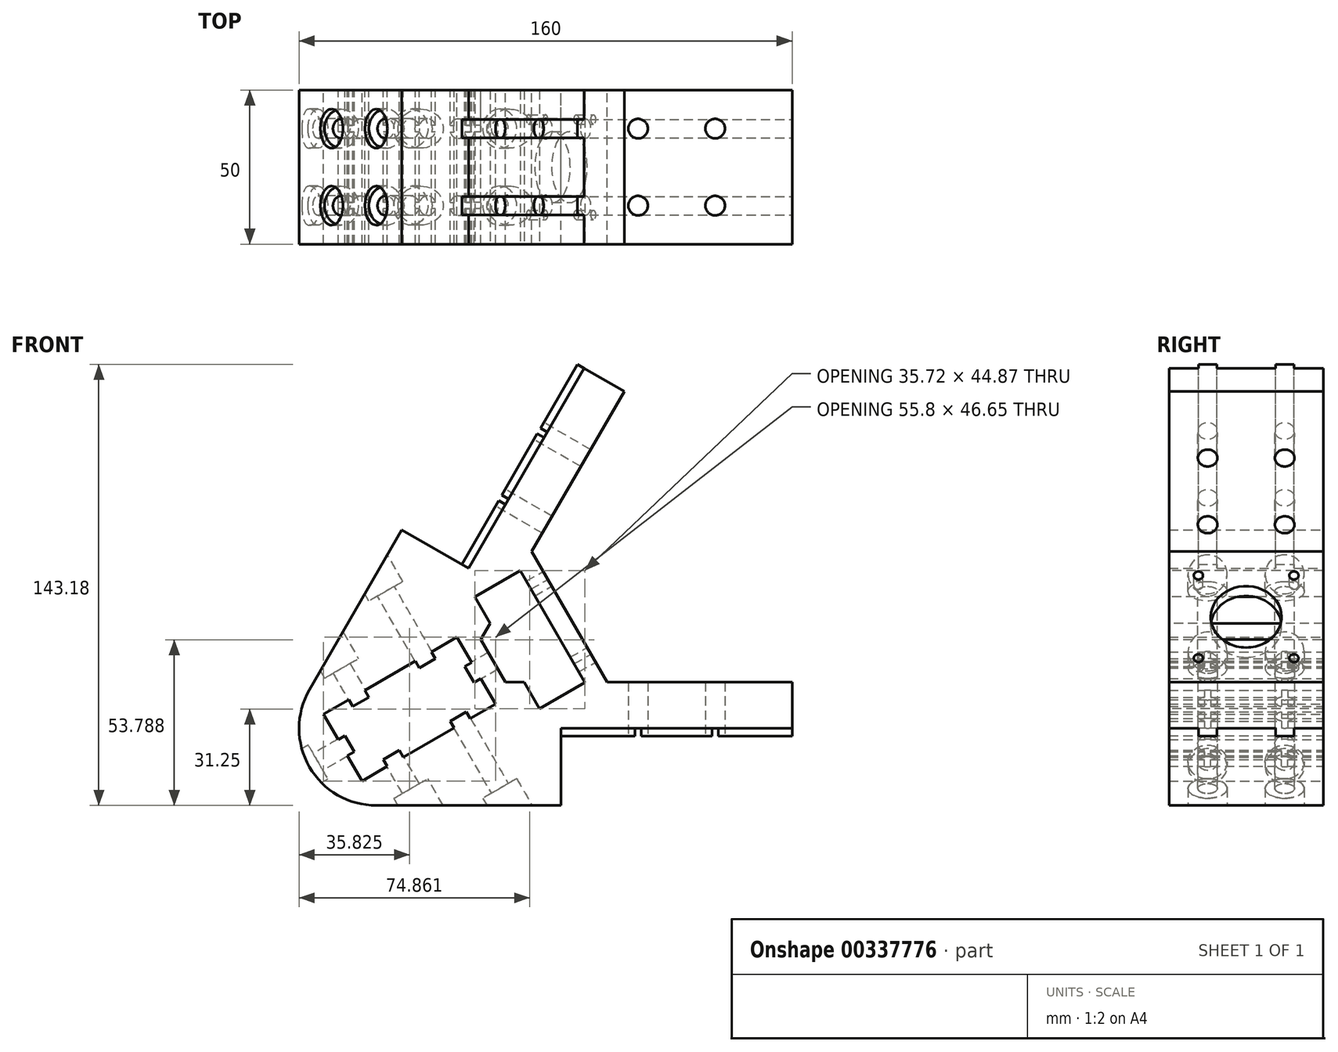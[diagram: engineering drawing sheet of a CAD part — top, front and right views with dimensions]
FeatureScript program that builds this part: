
annotation { "Feature Type Name" : "Feature", "Feature Type Description" : "" }
export const myFeature = defineFeature(function(context is Context, id is Id, definition is map)
    precondition{}
    {
        {
            var Q0;
            Q0=qCreatedBy(makeId("Front.planeOp"),FACE);
            var sketch = newSketch(context, id + "F0", { "sketchPlane" : qUnion([Q0])});
            skLineSegment(sketch, "E0", {"start": v(0, 0) * mm, "end": v(260, 0) * mm, "construction": true});
            skLineSegment(sketch, "E1", {"start": v(0, 0) * mm, "end": v(130, 225.17) * mm, "construction": true});
            skLineSegment(sketch, "E2", {"start": v(60, 0) * mm, "end": v(60, -25) * mm, "construction": true});
            skLineSegment(sketch, "E3", {"start": v(60, -25) * mm, "end": v(260, -25) * mm, "construction": true});
            skLineSegment(sketch, "E4", {"start": v(260, -25) * mm, "end": v(260, 0) * mm, "construction": true});
            skLineSegment(sketch, "E5", {"start": v(30, 51.96) * mm, "end": v(8.35, 64.46) * mm, "construction": true});
            skLineSegment(sketch, "E6", {"start": v(8.35, 64.46) * mm, "end": v(108.35, 237.67) * mm, "construction": true});
            skLineSegment(sketch, "E7", {"start": v(108.35, 237.67) * mm, "end": v(130, 225.17) * mm, "construction": true});
            skLineSegment(sketch, "E8", {"start": v(67.5, 116.91) * mm, "end": v(80.5, 109.41) * mm});
            skLineSegment(sketch, "E9", {"start": v(80.5, 109.41) * mm, "end": v(33.98, 28.85) * mm});
            skLineSegment(sketch, "E10", {"start": v(135, 0) * mm, "end": v(135, 15) * mm});
            skLineSegment(sketch, "E11", {"start": v(135, 15) * mm, "end": v(41.97, 15) * mm});
            skLineSegment(sketch, "E12", {"start": v(0, 0) * mm, "end": v(32.48, 18.75) * mm, "construction": true});
            skLineSegment(sketch, "E13", {"start": v(0, 0) * mm, "end": v(-6.25, 10.83) * mm, "construction": true});
            skLineSegment(sketch, "E14", {"start": v(32.48, 18.75) * mm, "end": v(26.23, 29.58) * mm});
            skLineSegment(sketch, "E15", {"start": v(26.23, 29.58) * mm, "end": v(-6.25, 10.83) * mm});
            skLineSegment(sketch, "E16", {"start": v(-6.25, 10.83) * mm, "end": v(-17.08, 4.58) * mm});
            skLineSegment(sketch, "E17", {"start": v(-17.08, 4.58) * mm, "end": v(-4.58, -17.08) * mm});
            skLineSegment(sketch, "E18", {"start": v(-4.58, -17.08) * mm, "end": v(38.73, 7.92) * mm});
            skLineSegment(sketch, "E19", {"start": v(38.73, 7.92) * mm, "end": v(32.48, 18.75) * mm});
            skArc(sketch, "E20", {"start": v(-21.65, 12.5) * mm, "mid": v(-21.65, -12.5) * mm, "end": v(0, -25) * mm});
            skLineSegment(sketch, "E21", {"start": v(8.35, 64.46) * mm, "end": v(-21.65, 12.5) * mm});
            skLineSegment(sketch, "E22", {"start": v(60, -25) * mm, "end": v(0, -25) * mm});
            skLineSegment(sketch, "E23", {"start": v(30, 51.96) * mm, "end": v(67.5, 116.91) * mm});
            skLineSegment(sketch, "E24", {"start": v(8.35, 64.46) * mm, "end": v(30, 51.96) * mm});
            skLineSegment(sketch, "E25", {"start": v(135, 0) * mm, "end": v(60, 0) * mm});
            skLineSegment(sketch, "E26", {"start": v(60, -25) * mm, "end": v(60, 0) * mm});
            skLineSegment(sketch, "E27", {"start": v(0, 0) * mm, "end": v(0, 0) * mm});
            skLineSegment(sketch, "E28", {"start": v(62.72, 36.21) * mm, "end": v(-21.65, -12.5) * mm});
            skLineSegment(sketch, "E29", {"start": v(50.47, 57.42) * mm, "end": v(74.97, 15) * mm});
            skLineSegment(sketch, "E30", {"start": v(46.8, 51.07) * mm, "end": v(67.64, 15) * mm});
            skLineSegment(sketch, "E31", {"start": v(41.97, 15) * mm, "end": v(33.98, 28.85) * mm});
            skLineSegment(sketch, "E32", {"start": v(46.72, 51.22) * mm, "end": v(32, 42.72) * mm, "construction": true});
            skLineSegment(sketch, "E33", {"start": v(32, 42.72) * mm, "end": v(53, 6.35) * mm, "construction": true});
            skLineSegment(sketch, "E34", {"start": v(53, 6.35) * mm, "end": v(67.72, 14.85) * mm, "construction": true});
            skLineSegment(sketch, "E35", {"start": v(57.22, 33.04) * mm, "end": v(42.5, 24.54) * mm});
            skSolve(sketch);
        }
        {
            var Q0;
            Q0=makeQuery(id+"F0.imprint","IMPRINT",FACE,{"disambiguationData":[TD([[makeQuery(id+"F0.imprint","IMPRINT",EDGE,{"derivedFrom":sQuery(id+"F0.wireOp",EDGE,"E8")}),-1.0]])]});
            var Q1;
            {var subQ0=sQuery(id+"F0.wireOp",EDGE,"E29");var subQ1=sQuery(id+"F0.wireOp",EDGE,"E9");var subQ2=makeQuery(id+"F0.imprint","INTERSECT",VERTEX,{"derivedFrom":[subQ1,subQ0]});Q1=makeQuery(id+"F0.imprint","IMPRINT",FACE,{"disambiguationData":[TD([[makeQuery(id+"F0.imprint","IMPRINT",EDGE,{"disambiguationData":[TD([[subQ2,-1.0]])],"derivedFrom":subQ1}),1.0]])]});}
            extrude(context, id + "F1", {"entities" : qUnion([Q0, Q1]), "depth" : 50 * mm});
        }
        {
            var Q0;
            Q0=makeQuery(id+"F1.opExtrude","CAP_FACE",FACE,{"disambiguationData":[OSD([sQuery(id+"F0.wireOp",EDGE,"E8"),sQuery(id+"F0.wireOp",EDGE,"E9"),sQuery(id+"F0.wireOp",EDGE,"E14"),sQuery(id+"F0.wireOp",EDGE,"E15"),sQuery(id+"F0.wireOp",EDGE,"E16"),sQuery(id+"F0.wireOp",EDGE,"E17"),sQuery(id+"F0.wireOp",EDGE,"E20"),sQuery(id+"F0.wireOp",EDGE,"E21"),sQuery(id+"F0.wireOp",EDGE,"oqZTHpmg-IY26-M5HD-25FB-tw3BaVAHPTJi"),sQuery(id+"F0.wireOp",EDGE,"E23"),sQuery(id+"F0.wireOp",EDGE,"E24"),sQuery(id+"F0.wireOp",EDGE,"E28"),sQuery(id+"F0.wireOp",EDGE,"E29"),sQuery(id+"F0.wireOp",EDGE,"E30"),sQuery(id+"F0.wireOp",EDGE,"hlFoshtQ-Obu4-Otg3-1oye-F89BNM93I3Rv")])],"isStart":true});
            var sketch = newSketch(context, id + "F2", { "sketchPlane" : qUnion([Q0])});
            skLineSegment(sketch, "E36.0", {"start": v(-26.23, 29.58) * mm, "end": v(17.08, 4.58) * mm});
            skLineSegment(sketch, "E37.0", {"start": v(-32.48, 18.75) * mm, "end": v(-26.23, 29.58) * mm});
            skLineSegment(sketch, "E38.0", {"start": v(17.08, 4.58) * mm, "end": v(10.83, -6.25) * mm});
            skLineSegment(sketch, "E39", {"start": v(-12.8, 21.83) * mm, "end": v(-14.07, 19.63) * mm});
            skLineSegment(sketch, "E40", {"start": v(-14.07, 19.63) * mm, "end": v(-19.27, 22.63) * mm});
            skLineSegment(sketch, "E41", {"start": v(-19.27, 22.63) * mm, "end": v(-18, 24.83) * mm});
            skLineSegment(sketch, "E42", {"start": v(-16.67, 21.13) * mm, "end": v(-15.4, 23.33) * mm});
            skLineSegment(sketch, "E43", {"start": v(10.83, -6.25) * mm, "end": v(8.63, -4.98) * mm});
            skLineSegment(sketch, "E44", {"start": v(8.63, -4.98) * mm, "end": v(10.13, -2.38) * mm});
            skLineSegment(sketch, "E45", {"start": v(10.13, -2.38) * mm, "end": v(12.33, -3.65) * mm});
            skLineSegment(sketch, "E46", {"start": v(-32.48, 18.75) * mm, "end": v(-30.28, 17.48) * mm});
            skLineSegment(sketch, "E47", {"start": v(-30.28, 17.48) * mm, "end": v(-28.78, 20.08) * mm});
            skLineSegment(sketch, "E48", {"start": v(-28.78, 20.08) * mm, "end": v(-30.98, 21.35) * mm});
            skLineSegment(sketch, "E49", {"start": v(8.85, 9.33) * mm, "end": v(7.58, 7.13) * mm});
            skLineSegment(sketch, "E50", {"start": v(7.58, 7.13) * mm, "end": v(2.38, 10.13) * mm});
            skLineSegment(sketch, "E51", {"start": v(2.38, 10.13) * mm, "end": v(3.65, 12.33) * mm});
            skLineSegment(sketch, "E52", {"start": v(4.98, 8.63) * mm, "end": v(6.25, 10.83) * mm});
            skSolve(sketch);
        }
        {
            var Q0;
            {var subQ0=sQuery(id+"F2.wireOp",EDGE,"E41");Q0=makeQuery(id+"F2.imprint","IMPRINT",FACE,{"disambiguationData":[TD([[makeQuery(id+"F2.imprint","IMPRINT",EDGE,{"derivedFrom":subQ0}),-1.0]])]});}
            var Q1;
            {var subQ0=sQuery(id+"F2.wireOp",EDGE,"E39");Q1=makeQuery(id+"F2.imprint","IMPRINT",FACE,{"disambiguationData":[TD([[makeQuery(id+"F2.imprint","IMPRINT",EDGE,{"derivedFrom":subQ0}),-1.0]])]});}
            var Q2;
            {var subQ0=sQuery(id+"F2.wireOp",EDGE,"E46");Q2=makeQuery(id+"F2.imprint","IMPRINT",FACE,{"disambiguationData":[TD([[makeQuery(id+"F2.imprint","IMPRINT",EDGE,{"derivedFrom":subQ0}),1.0]])]});}
            var Q3;
            {var subQ0=sQuery(id+"F2.wireOp",EDGE,"E43");Q3=makeQuery(id+"F2.imprint","IMPRINT",FACE,{"disambiguationData":[TD([[makeQuery(id+"F2.imprint","IMPRINT",EDGE,{"derivedFrom":subQ0}),-1.0]])]});}
            var Q4;
            {var subQ0=sQuery(id+"F2.wireOp",EDGE,"E51");Q4=makeQuery(id+"F2.imprint","IMPRINT",FACE,{"disambiguationData":[TD([[makeQuery(id+"F2.imprint","IMPRINT",EDGE,{"derivedFrom":subQ0}),-1.0]])]});}
            var Q5;
            {var subQ0=sQuery(id+"F2.wireOp",EDGE,"E49");Q5=makeQuery(id+"F2.imprint","IMPRINT",FACE,{"disambiguationData":[TD([[makeQuery(id+"F2.imprint","IMPRINT",EDGE,{"derivedFrom":subQ0}),-1.0]])]});}
            var Q6;
            Q6=makeQuery(id+"F1.opExtrude","CAP_FACE",FACE,{"disambiguationData":[OSD([sQuery(id+"F0.wireOp",EDGE,"E8"),sQuery(id+"F0.wireOp",EDGE,"E9"),sQuery(id+"F0.wireOp",EDGE,"E14"),sQuery(id+"F0.wireOp",EDGE,"E15"),sQuery(id+"F0.wireOp",EDGE,"E16"),sQuery(id+"F0.wireOp",EDGE,"E17"),sQuery(id+"F0.wireOp",EDGE,"E20"),sQuery(id+"F0.wireOp",EDGE,"E21"),sQuery(id+"F0.wireOp",EDGE,"oqZTHpmg-IY26-M5HD-25FB-tw3BaVAHPTJi"),sQuery(id+"F0.wireOp",EDGE,"E23"),sQuery(id+"F0.wireOp",EDGE,"E24"),sQuery(id+"F0.wireOp",EDGE,"E28"),sQuery(id+"F0.wireOp",EDGE,"E29"),sQuery(id+"F0.wireOp",EDGE,"E30"),sQuery(id+"F0.wireOp",EDGE,"hlFoshtQ-Obu4-Otg3-1oye-F89BNM93I3Rv")])],"isStart":false});
            extrude(context, id + "F3", {"entities" : qUnion([Q0, Q1, Q2, Q3, Q4, Q5]), "operationType" : NewBodyOperationType.ADD, "endBound" : BoundingType.UP_TO_SURFACE, "oppositeDirection" : true, "endBoundEntityFace" : qUnion([Q6]), "depth" : 25.4 * mm, "offsetDistance" : 25.4 * mm});
        }
        {
            var Q0;
            Q0=makeQuery(id+"F1.opExtrude","SWEPT_FACE",FACE,{"disambiguationData":[OSD([sQuery(id+"F0.wireOp",EDGE,"E23")])]});
            var sketch = newSketch(context, id + "F4", { "sketchPlane" : qUnion([Q0])});
            skLineSegment(sketch, "E53.bottom", {"start": v(15.5, 60) * mm, "end": v(9.5, 60) * mm});
            skLineSegment(sketch, "E53.top", {"start": v(15.5, 135) * mm, "end": v(9.5, 135) * mm});
            skLineSegment(sketch, "E53.left", {"start": v(15.5, 60) * mm, "end": v(15.5, 135) * mm});
            skLineSegment(sketch, "E53.right", {"start": v(9.5, 60) * mm, "end": v(9.5, 135) * mm});
            skPoint(sketch, "E53.middle", {"position": v(12.5, 97.5) * mm});
            skLineSegment(sketch, "E54.bottom", {"start": v(34.5, 60) * mm, "end": v(40.5, 60) * mm});
            skLineSegment(sketch, "E54.top", {"start": v(34.5, 135) * mm, "end": v(40.5, 135) * mm});
            skLineSegment(sketch, "E54.left", {"start": v(40.5, 60) * mm, "end": v(40.5, 135) * mm});
            skLineSegment(sketch, "E54.right", {"start": v(34.5, 60) * mm, "end": v(34.5, 135) * mm});
            skPoint(sketch, "E54.middle", {"position": v(37.5, 97.5) * mm});
            skSolve(sketch);
        }
        {
            var Q0;
            Q0 = qSketchRegion(id + "F4", true);
            extrude(context, id + "F5", {"entities" : qUnion([Q0]), "operationType" : NewBodyOperationType.ADD, "depth" : 2.54 * mm});
        }
        {
            var Q0;
            Q0=makeQuery(id+"F5.opExtrude","CAP_FACE",FACE,{"disambiguationData":[OSD([sQuery(id+"F4.wireOp",EDGE,"E53.bottom"),sQuery(id+"F4.wireOp",EDGE,"E53.top"),sQuery(id+"F4.wireOp",EDGE,"E53.left"),sQuery(id+"F4.wireOp",EDGE,"E53.right")])],"isStart":false});
            var sketch = newSketch(context, id + "F6", { "sketchPlane" : qUnion([Q0])});
            skLineSegment(sketch, "E55", {"start": v(12.5, 60) * mm, "end": v(12.5, 85) * mm});
            skLineSegment(sketch, "E56", {"start": v(12.5, 85) * mm, "end": v(12.5, 110) * mm});
            skLineSegment(sketch, "E57", {"start": v(12.5, 110) * mm, "end": v(12.5, 135) * mm});
            skLineSegment(sketch, "E58.0", {"start": v(40.5, 60) * mm, "end": v(34.5, 60) * mm});
            skLineSegment(sketch, "E59.0", {"start": v(40.5, 135) * mm, "end": v(34.5, 135) * mm});
            skLineSegment(sketch, "E60", {"start": v(37.5, 60) * mm, "end": v(37.5, 85) * mm});
            skLineSegment(sketch, "E61", {"start": v(37.5, 85) * mm, "end": v(37.5, 110) * mm});
            skLineSegment(sketch, "E62", {"start": v(37.5, 110) * mm, "end": v(37.5, 135) * mm});
            skCircle(sketch, "E63", {"center": v(12.5, 85) * mm, "radius": 3.18 * mm});
            skCircle(sketch, "E64", {"center": v(12.5, 110) * mm, "radius": 3.18 * mm});
            skCircle(sketch, "E65", {"center": v(37.5, 110) * mm, "radius": 3.18 * mm});
            skCircle(sketch, "E66", {"center": v(37.5, 85) * mm, "radius": 3.18 * mm});
            skSolve(sketch);
        }
        {
            var Q0;
            Q0 = qSketchRegion(id + "F6", true);
            extrude(context, id + "F7", {"entities" : qUnion([Q0]), "operationType" : NewBodyOperationType.REMOVE, "endBound" : BoundingType.THROUGH_ALL, "oppositeDirection" : true, "depth" : 25.4 * mm});
        }
        {
            var Q0;
            {var subQ0=sQuery(id+"F0.wireOp",EDGE,"E28");Q0=makeQuery(id+"F3.boolean.opBoolean","MERGE",FACE,{"derivedFrom":[makeQuery(id+"F1.opExtrude","SWEPT_FACE",FACE,{"disambiguationData":[OSD([subQ0]),TDD([makeQuery(id+"F0.imprint","IMPRINT",EDGE,{"disambiguationData":[TD([[makeQuery(id+"F0.imprint","INTERSECT",VERTEX,{"derivedFrom":[sQuery(id+"F0.wireOp",EDGE,"E20"),subQ0]}),1.0]])],"derivedFrom":subQ0})])]}),makeQuery(id+"F3.opExtrude","SWEPT_FACE",FACE,{"disambiguationData":[OSD([sQuery(id+"F2.wireOp",EDGE,"E43")])]})]});}
            var sketch = newSketch(context, id + "F8", { "sketchPlane" : qUnion([Q0])});
            skLineSegment(sketch, "E67", {"start": v(-9.96, 12.5) * mm, "end": v(-25, 12.5) * mm});
            skLineSegment(sketch, "E68", {"start": v(-25, 6.15) * mm, "end": v(-21.83, 6.15) * mm});
            skLineSegment(sketch, "E69", {"start": v(-21.83, 6.15) * mm, "end": v(-21.83, 9.32) * mm});
            skLineSegment(sketch, "E70", {"start": v(-21.83, 9.32) * mm, "end": v(-9.96, 9.33) * mm});
            skLineSegment(sketch, "E71", {"start": v(-25, 6.15) * mm, "end": v(-25, 12.5) * mm});
            skLineSegment(sketch, "E72", {"start": v(-9.96, 37.5) * mm, "end": v(-25, 37.5) * mm});
            skLineSegment(sketch, "E73", {"start": v(-25, 37.5) * mm, "end": v(-25, 31.15) * mm});
            skLineSegment(sketch, "E74", {"start": v(-25, 31.15) * mm, "end": v(-21.82, 31.15) * mm});
            skLineSegment(sketch, "E75", {"start": v(-21.83, 31.15) * mm, "end": v(-21.83, 34.33) * mm});
            skLineSegment(sketch, "E76", {"start": v(-21.83, 34.33) * mm, "end": v(-9.96, 34.33) * mm});
            skLineSegment(sketch, "E77.0", {"start": v(43.85, 50) * mm, "end": v(43.85, 0) * mm});
            skLineSegment(sketch, "E78", {"start": v(-9.96, 37.5) * mm, "end": v(43.85, 37.5) * mm});
            skLineSegment(sketch, "E79", {"start": v(-9.96, 12.5) * mm, "end": v(43.85, 12.5) * mm});
            skLineSegment(sketch, "E80", {"start": v(43.85, 12.5) * mm, "end": v(43.85, 9.33) * mm});
            skLineSegment(sketch, "E81", {"start": v(43.85, 9.33) * mm, "end": v(-9.96, 9.33) * mm});
            skLineSegment(sketch, "E82", {"start": v(-9.96, 34.33) * mm, "end": v(43.85, 34.33) * mm});
            skLineSegment(sketch, "E83", {"start": v(43.85, 34.33) * mm, "end": v(43.85, 37.5) * mm});
            skLineSegment(sketch, "E84", {"start": v(-25, 25) * mm, "end": v(-16.63, 25) * mm, "construction": true});
            skSolve(sketch);
        }
        {
            var Q0;
            {var subQ0=sQuery(id+"F8.wireOp",EDGE,"E67");Q0=makeQuery(id+"F8.imprint","IMPRINT",FACE,{"disambiguationData":[TD([[makeQuery(id+"F8.imprint","IMPRINT",EDGE,{"derivedFrom":subQ0}),1.0]])]});}
            var Q1;
            {var subQ0=sQuery(id+"F8.wireOp",EDGE,"E79");Q1=makeQuery(id+"F8.imprint","IMPRINT",FACE,{"disambiguationData":[TD([[makeQuery(id+"F8.imprint","IMPRINT",EDGE,{"derivedFrom":subQ0}),-1.0]])]});}
            var Q2;
            Q2=sQuery(id+"F8.wireOp",EDGE,"E67");
            revolve(context, id + "F9", {"operationType" : NewBodyOperationType.REMOVE, "entities" : qUnion([Q0, Q1]), "axis" : qUnion([Q2]), "revolveType" : RevolveType.FULL, "oppositeDirection" : true});
        }
        {
            var Q0;
            {var subQ0=sQuery(id+"F8.wireOp",EDGE,"E72");Q0=makeQuery(id+"F8.imprint","IMPRINT",FACE,{"disambiguationData":[TD([[makeQuery(id+"F8.imprint","IMPRINT",EDGE,{"derivedFrom":subQ0}),1.0]])]});}
            var Q1;
            {var subQ0=sQuery(id+"F8.wireOp",EDGE,"E78");Q1=makeQuery(id+"F8.imprint","IMPRINT",FACE,{"disambiguationData":[TD([[makeQuery(id+"F8.imprint","IMPRINT",EDGE,{"derivedFrom":subQ0}),-1.0]])]});}
            var Q2;
            Q2=sQuery(id+"F8.wireOp",EDGE,"E72");
            revolve(context, id + "F10", {"operationType" : NewBodyOperationType.REMOVE, "entities" : qUnion([Q0, Q1]), "axis" : qUnion([Q2]), "revolveType" : RevolveType.FULL, "oppositeDirection" : true});
        }
        {
            var Q0;
            {var subQ0=sQuery(id+"F2.wireOp",EDGE,"E36.0");Q0=makeQuery(id+"F3.boolean.opBoolean","MERGE",FACE,{"derivedFrom":[makeQuery(id+"F1.opExtrude","CAP_FACE",FACE,{"disambiguationData":[OSD([sQuery(id+"F0.wireOp",EDGE,"E8"),sQuery(id+"F0.wireOp",EDGE,"E9"),sQuery(id+"F0.wireOp",EDGE,"E14"),sQuery(id+"F0.wireOp",EDGE,"E15"),sQuery(id+"F0.wireOp",EDGE,"E16"),sQuery(id+"F0.wireOp",EDGE,"E17"),sQuery(id+"F0.wireOp",EDGE,"E20"),sQuery(id+"F0.wireOp",EDGE,"E21"),sQuery(id+"F0.wireOp",EDGE,"E23"),sQuery(id+"F0.wireOp",EDGE,"E24"),sQuery(id+"F0.wireOp",EDGE,"E28"),sQuery(id+"F0.wireOp",EDGE,"E29"),sQuery(id+"F0.wireOp",EDGE,"E30"),sQuery(id+"F0.wireOp",EDGE,"E31")])],"isStart":true}),makeQuery(id+"F3.opExtrude","CAP_FACE",FACE,{"disambiguationData":[OSD([subQ0,sQuery(id+"F2.wireOp",EDGE,"E39"),sQuery(id+"F2.wireOp",EDGE,"E40"),sQuery(id+"F2.wireOp",EDGE,"E41")])],"isStart":true}),makeQuery(id+"F3.opExtrude","CAP_FACE",FACE,{"disambiguationData":[OSD([subQ0,sQuery(id+"F2.wireOp",EDGE,"E49"),sQuery(id+"F2.wireOp",EDGE,"E50"),sQuery(id+"F2.wireOp",EDGE,"E51")])],"isStart":true}),makeQuery(id+"F3.opExtrude","CAP_FACE",FACE,{"disambiguationData":[OSD([sQuery(id+"F2.wireOp",EDGE,"E37.0"),sQuery(id+"F2.wireOp",EDGE,"E46"),sQuery(id+"F2.wireOp",EDGE,"E47"),sQuery(id+"F2.wireOp",EDGE,"E48")])],"isStart":true}),makeQuery(id+"F3.opExtrude","CAP_FACE",FACE,{"disambiguationData":[OSD([sQuery(id+"F2.wireOp",EDGE,"E38.0"),sQuery(id+"F2.wireOp",EDGE,"E43"),sQuery(id+"F2.wireOp",EDGE,"E44"),sQuery(id+"F2.wireOp",EDGE,"E45")])],"isStart":true})]});}
            var sketch = newSketch(context, id + "F11", { "sketchPlane" : qUnion([Q0])});
            skLineSegment(sketch, "E85", {"start": v(-16.67, 21.13) * mm, "end": v(-15.4, 23.33) * mm, "construction": true});
            skSolve(sketch);
        }
        {
            var Q0;
            Q0=sQuery(id+"F11.wireOp",EDGE,"E85");
            var Q1;
            {var subQ15=sQuery(id+"F0.wireOp",EDGE,"E8");Q1=makeQuery(id+"F11.imprint","IMPRINT",FACE,{"disambiguationData":[TD([[makeQuery(id+"F11.imprint","IMPRINT",EDGE,{"derivedFrom":makeQuery(id+"F1.opExtrude","CAP_EDGE",EDGE,{"disambiguationData":[OSD([subQ15])],"isStart":true})}),1.0]])]});}
            cPlane(context, id + "F12", {"entities" : qUnion([Q0, Q1]), "cplaneType" : CPlaneType.LINE_ANGLE, "offset" : 25.4 * mm, "angle" : 90 * degree, "width" : 152.4 * mm, "height" : 152.4 * mm});
        }
        {
            var Q0;
            Q0=qCreatedBy(id+"F12.planeOp",FACE);
            var sketch = newSketch(context, id + "F13", { "sketchPlane" : qUnion([Q0])});
            skLineSegment(sketch, "E86", {"start": v(0, 9.96) * mm, "end": v(0, 43.3) * mm});
            skLineSegment(sketch, "E87", {"start": v(-50, 43.3) * mm, "end": v(-50, 9.96) * mm});
            skLineSegment(sketch, "E88", {"start": v(0, 43.3) * mm, "end": v(-12.5, 43.3) * mm});
            skLineSegment(sketch, "E89", {"start": v(-12.5, 43.3) * mm, "end": v(-37.5, 43.3) * mm});
            skLineSegment(sketch, "E90", {"start": v(-37.5, 43.3) * mm, "end": v(-50, 43.3) * mm});
            skLineSegment(sketch, "E91", {"start": v(0, 9.96) * mm, "end": v(-12.5, 9.96) * mm});
            skLineSegment(sketch, "E92", {"start": v(-12.5, 9.96) * mm, "end": v(-37.5, 9.96) * mm});
            skLineSegment(sketch, "E93", {"start": v(-37.5, 9.96) * mm, "end": v(-50, 9.96) * mm});
            skLineSegment(sketch, "E94", {"start": v(-12.5, 9.96) * mm, "end": v(-12.5, 43.3) * mm});
            skLineSegment(sketch, "E95", {"start": v(-12.5, 49.65) * mm, "end": v(-6.15, 49.65) * mm});
            skLineSegment(sketch, "E96", {"start": v(-6.15, 49.65) * mm, "end": v(-6.15, 36.95) * mm});
            skLineSegment(sketch, "E97", {"start": v(-6.15, 36.95) * mm, "end": v(-9.33, 36.95) * mm});
            skLineSegment(sketch, "E98", {"start": v(-9.33, 36.95) * mm, "end": v(-9.33, 9.96) * mm});
            skLineSegment(sketch, "E99", {"start": v(-12.5, 49.65) * mm, "end": v(-12.5, 43.3) * mm});
            skLineSegment(sketch, "E100", {"start": v(-37.5, 9.96) * mm, "end": v(-37.5, 49.65) * mm});
            skLineSegment(sketch, "E101", {"start": v(-37.5, 49.65) * mm, "end": v(-31.15, 49.65) * mm});
            skLineSegment(sketch, "E102", {"start": v(-31.15, 49.65) * mm, "end": v(-31.15, 36.95) * mm});
            skLineSegment(sketch, "E103", {"start": v(-31.15, 36.95) * mm, "end": v(-34.33, 36.95) * mm});
            skLineSegment(sketch, "E104", {"start": v(-34.33, 36.95) * mm, "end": v(-34.33, 9.96) * mm});
            skLineSegment(sketch, "E105", {"start": v(-34.33, 9.96) * mm, "end": v(-37.5, 9.96) * mm});
            skSolve(sketch);
        }
        {
            var Q0;
            {var subQ4=sQuery(id+"F13.wireOp",EDGE,"E95");Q0=makeQuery(id+"F13.imprint","IMPRINT",FACE,{"disambiguationData":[TD([[makeQuery(id+"F13.imprint","IMPRINT",EDGE,{"derivedFrom":subQ4}),-1.0]])]});}
            var Q1;
            {var subQ4=sQuery(id+"F13.wireOp",EDGE,"E94");Q1=makeQuery(id+"F13.imprint","IMPRINT",FACE,{"disambiguationData":[TD([[makeQuery(id+"F13.imprint","IMPRINT",EDGE,{"derivedFrom":subQ4}),-1.0]])]});}
            var Q2;
            Q2=sQuery(id+"F13.wireOp",EDGE,"E94");
            revolve(context, id + "F14", {"operationType" : NewBodyOperationType.REMOVE, "entities" : qUnion([Q0, Q1]), "axis" : qUnion([Q2]), "revolveType" : RevolveType.FULL, "oppositeDirection" : true});
        }
        {
            var Q0;
            {var subQ5=sQuery(id+"F13.wireOp",EDGE,"E101");Q0=makeQuery(id+"F13.imprint","IMPRINT",FACE,{"disambiguationData":[TD([[makeQuery(id+"F13.imprint","IMPRINT",EDGE,{"derivedFrom":subQ5}),-1.0]])]});}
            var Q1;
            {var subQ0=sQuery(id+"F13.wireOp",EDGE,"E103");Q1=makeQuery(id+"F13.imprint","IMPRINT",FACE,{"disambiguationData":[TD([[makeQuery(id+"F13.imprint","IMPRINT",EDGE,{"derivedFrom":subQ0}),-1.0]])]});}
            var Q2;
            Q2=sQuery(id+"F13.wireOp",EDGE,"E100");
            revolve(context, id + "F15", {"operationType" : NewBodyOperationType.REMOVE, "entities" : qUnion([Q0, Q1]), "axis" : qUnion([Q2]), "revolveType" : RevolveType.FULL, "oppositeDirection" : true});
        }
        {
            var Q0;
            Q0=makeQuery(id+"F1.opExtrude","SWEPT_FACE",FACE,{"disambiguationData":[OSD([sQuery(id+"F0.wireOp",EDGE,"E29")])]});
            var sketch = newSketch(context, id + "F16", { "sketchPlane" : qUnion([Q0])});
            skLineSegment(sketch, "E106.bottom", {"start": v(-9.5, 15.5) * mm, "end": v(-40.5, 15.5) * mm});
            skLineSegment(sketch, "E106.top", {"start": v(-9.5, -15.5) * mm, "end": v(-40.5, -15.5) * mm});
            skLineSegment(sketch, "E106.left", {"start": v(-9.5, 15.5) * mm, "end": v(-9.5, -15.5) * mm});
            skLineSegment(sketch, "E106.right", {"start": v(-40.5, 15.5) * mm, "end": v(-40.5, -15.5) * mm});
            skPoint(sketch, "E106.middle", {"position": v(-25, 0) * mm});
            skCircle(sketch, "E107", {"center": v(-9.5, 15.5) * mm, "radius": 1.5 * mm});
            skCircle(sketch, "E108", {"center": v(-40.5, 15.5) * mm, "radius": 1.5 * mm});
            skCircle(sketch, "E109", {"center": v(-25, 0) * mm, "radius": 11.5 * mm});
            skSolve(sketch);
        }
        {
            var Q0;
            {var subQ0=sQuery(id+"F16.wireOp",EDGE,"E106.left");var subQ1=sQuery(id+"F16.wireOp",EDGE,"E106.bottom");var subQ2=makeQuery(id+"F16.imprint","INTERSECT",VERTEX,{"derivedFrom":[subQ1,subQ0]});Q0=makeQuery(id+"F16.imprint","IMPRINT",FACE,{"disambiguationData":[TD([[makeQuery(id+"F16.imprint","IMPRINT",EDGE,{"disambiguationData":[TD([[subQ2,-1.0]])],"derivedFrom":subQ1}),-1.0]])]});}
            var Q1;
            {var subQ0=sQuery(id+"F16.wireOp",EDGE,"E106.left");var subQ1=sQuery(id+"F16.wireOp",EDGE,"E106.bottom");var subQ2=makeQuery(id+"F16.imprint","INTERSECT",VERTEX,{"derivedFrom":[subQ1,subQ0]});Q1=makeQuery(id+"F16.imprint","IMPRINT",FACE,{"disambiguationData":[TD([[makeQuery(id+"F16.imprint","IMPRINT",EDGE,{"disambiguationData":[TD([[subQ2,-1.0]])],"derivedFrom":subQ1}),1.0]])]});}
            var Q2;
            {var subQ0=sQuery(id+"F16.wireOp",EDGE,"E106.right");var subQ1=sQuery(id+"F16.wireOp",EDGE,"E106.bottom");var subQ2=makeQuery(id+"F16.imprint","INTERSECT",VERTEX,{"derivedFrom":[subQ1,subQ0]});Q2=makeQuery(id+"F16.imprint","IMPRINT",FACE,{"disambiguationData":[TD([[makeQuery(id+"F16.imprint","IMPRINT",EDGE,{"disambiguationData":[TD([[subQ2,1.0]])],"derivedFrom":subQ1}),1.0]])]});}
            var Q3;
            {var subQ0=sQuery(id+"F16.wireOp",EDGE,"E106.right");var subQ1=sQuery(id+"F16.wireOp",EDGE,"E106.bottom");var subQ2=makeQuery(id+"F16.imprint","INTERSECT",VERTEX,{"derivedFrom":[subQ1,subQ0]});Q3=makeQuery(id+"F16.imprint","IMPRINT",FACE,{"disambiguationData":[TD([[makeQuery(id+"F16.imprint","IMPRINT",EDGE,{"disambiguationData":[TD([[subQ2,1.0]])],"derivedFrom":subQ1}),-1.0]])]});}
            var Q4;
            {var subQ0=sQuery(id+"F16.wireOp",EDGE,"E109");var subQ1=makeQuery(id+"F1.opExtrude","SWEPT_EDGE",EDGE,{"disambiguationData":[OSD([sQuery(id+"F0.wireOp",EDGE,"E28"),sQuery(id+"F0.wireOp",EDGE,"E29")])]});var subQ2=makeQuery(id+"F16.imprint","INTERSECT",VERTEX,{"disambiguationData":[OD(0.0)],"derivedFrom":[subQ1,subQ0]});Q4=makeQuery(id+"F16.imprint","IMPRINT",FACE,{"disambiguationData":[TD([[makeQuery(id+"F16.imprint","IMPRINT",EDGE,{"disambiguationData":[TD([[subQ2,-1.0]])],"derivedFrom":subQ0}),1.0]])]});}
            var Q5;
            Q5=makeQuery(id+"F1.opExtrude","SWEPT_FACE",FACE,{"disambiguationData":[OSD([sQuery(id+"F0.wireOp",EDGE,"E30")])]});
            extrude(context, id + "F17", {"entities" : qUnion([Q0, Q1, Q2, Q3, Q4]), "operationType" : NewBodyOperationType.REMOVE, "endBound" : BoundingType.UP_TO_SURFACE, "oppositeDirection" : true, "endBoundEntityFace" : qUnion([Q5]), "depth" : 25.4 * mm});
        }
        {
            var Q0;
            {var subQ0=sQuery(id+"F2.wireOp",EDGE,"E36.0");Q0=makeQuery(id+"F3.boolean.opBoolean","MERGE",FACE,{"derivedFrom":[makeQuery(id+"F1.opExtrude","CAP_FACE",FACE,{"disambiguationData":[OSD([sQuery(id+"F0.wireOp",EDGE,"E8"),sQuery(id+"F0.wireOp",EDGE,"E9"),sQuery(id+"F0.wireOp",EDGE,"E14"),sQuery(id+"F0.wireOp",EDGE,"E15"),sQuery(id+"F0.wireOp",EDGE,"E16"),sQuery(id+"F0.wireOp",EDGE,"E17"),sQuery(id+"F0.wireOp",EDGE,"E20"),sQuery(id+"F0.wireOp",EDGE,"E21"),sQuery(id+"F0.wireOp",EDGE,"E23"),sQuery(id+"F0.wireOp",EDGE,"E24"),sQuery(id+"F0.wireOp",EDGE,"E28"),sQuery(id+"F0.wireOp",EDGE,"E29"),sQuery(id+"F0.wireOp",EDGE,"E30"),sQuery(id+"F0.wireOp",EDGE,"E31")])],"isStart":false}),makeQuery(id+"F3.opExtrude","CAP_FACE",FACE,{"disambiguationData":[OSD([subQ0,sQuery(id+"F2.wireOp",EDGE,"E39"),sQuery(id+"F2.wireOp",EDGE,"E40"),sQuery(id+"F2.wireOp",EDGE,"E41")])],"isStart":false}),makeQuery(id+"F3.opExtrude","CAP_FACE",FACE,{"disambiguationData":[OSD([subQ0,sQuery(id+"F2.wireOp",EDGE,"E49"),sQuery(id+"F2.wireOp",EDGE,"E50"),sQuery(id+"F2.wireOp",EDGE,"E51")])],"isStart":false}),makeQuery(id+"F3.opExtrude","CAP_FACE",FACE,{"disambiguationData":[OSD([sQuery(id+"F2.wireOp",EDGE,"E37.0"),sQuery(id+"F2.wireOp",EDGE,"E46"),sQuery(id+"F2.wireOp",EDGE,"E47"),sQuery(id+"F2.wireOp",EDGE,"E48")])],"isStart":false}),makeQuery(id+"F3.opExtrude","CAP_FACE",FACE,{"disambiguationData":[OSD([sQuery(id+"F2.wireOp",EDGE,"E38.0"),sQuery(id+"F2.wireOp",EDGE,"E43"),sQuery(id+"F2.wireOp",EDGE,"E44"),sQuery(id+"F2.wireOp",EDGE,"E45")])],"isStart":false})]});}
            var sketch = newSketch(context, id + "F18", { "sketchPlane" : qUnion([Q0])});
            skLineSegment(sketch, "E110.0", {"start": v(32, 42.72) * mm, "end": v(53, 6.35) * mm});
            skLineSegment(sketch, "E111.0", {"start": v(46.72, 51.22) * mm, "end": v(32, 42.72) * mm});
            skLineSegment(sketch, "E112.0.0", {"start": v(33.98, 28.85) * mm, "end": v(46.8, 51.07) * mm});
            skLineSegment(sketch, "E112.0.1", {"start": v(46.8, 51.07) * mm, "end": v(57.22, 33.04) * mm});
            skLineSegment(sketch, "E112.0.2", {"start": v(57.22, 33.04) * mm, "end": v(62.72, 36.21) * mm});
            skLineSegment(sketch, "E112.0.3", {"start": v(62.72, 36.21) * mm, "end": v(50.47, 57.43) * mm});
            skLineSegment(sketch, "E112.0.4", {"start": v(50.47, 57.43) * mm, "end": v(80.5, 109.41) * mm});
            skLineSegment(sketch, "E112.0.5", {"start": v(80.5, 109.41) * mm, "end": v(67.5, 116.91) * mm});
            skLineSegment(sketch, "E112.0.6", {"start": v(67.5, 116.91) * mm, "end": v(30, 51.96) * mm});
            skLineSegment(sketch, "E112.0.7", {"start": v(30, 51.96) * mm, "end": v(8.35, 64.46) * mm});
            skLineSegment(sketch, "E112.0.8", {"start": v(8.35, 64.46) * mm, "end": v(-21.65, 12.5) * mm});
            skLineSegment(sketch, "E112.0.9", {"start": v(-21.65, 12.5) * mm, "end": v(-21.65, 12.5) * mm});
            skLineSegment(sketch, "E112.0.11", {"start": v(-8.63, -4.98) * mm, "end": v(-10.13, -2.38) * mm});
            skLineSegment(sketch, "E112.0.12", {"start": v(-10.13, -2.38) * mm, "end": v(-12.33, -3.65) * mm});
            skLineSegment(sketch, "E112.0.13", {"start": v(-12.33, -3.65) * mm, "end": v(-17.08, 4.58) * mm});
            skLineSegment(sketch, "E112.0.14", {"start": v(-17.08, 4.58) * mm, "end": v(-8.85, 9.33) * mm});
            skLineSegment(sketch, "E112.0.15", {"start": v(-8.85, 9.33) * mm, "end": v(-7.58, 7.13) * mm});
            skLineSegment(sketch, "E112.0.16", {"start": v(-7.58, 7.13) * mm, "end": v(-2.38, 10.13) * mm});
            skLineSegment(sketch, "E112.0.17", {"start": v(-2.38, 10.13) * mm, "end": v(-3.65, 12.33) * mm});
            skLineSegment(sketch, "E112.0.18", {"start": v(-3.65, 12.33) * mm, "end": v(12.8, 21.83) * mm});
            skLineSegment(sketch, "E112.0.19", {"start": v(12.8, 21.83) * mm, "end": v(14.07, 19.63) * mm});
            skLineSegment(sketch, "E112.0.20", {"start": v(14.07, 19.63) * mm, "end": v(19.27, 22.63) * mm});
            skLineSegment(sketch, "E112.0.21", {"start": v(19.27, 22.63) * mm, "end": v(18, 24.83) * mm});
            skLineSegment(sketch, "E112.0.22", {"start": v(18, 24.83) * mm, "end": v(26.23, 29.58) * mm});
            skLineSegment(sketch, "E112.0.23", {"start": v(26.23, 29.58) * mm, "end": v(30.98, 21.35) * mm});
            skLineSegment(sketch, "E112.0.24", {"start": v(30.98, 21.35) * mm, "end": v(28.78, 20.08) * mm});
            skLineSegment(sketch, "E112.0.25", {"start": v(28.78, 20.08) * mm, "end": v(30.28, 17.48) * mm});
            skLineSegment(sketch, "E112.0.26", {"start": v(30.28, 17.48) * mm, "end": v(37.98, 21.92) * mm});
            skLineSegment(sketch, "E112.0.27", {"start": v(37.98, 21.92) * mm, "end": v(33.98, 28.85) * mm});
            skLineSegment(sketch, "E113", {"start": v(46.8, 51.07) * mm, "end": v(46.72, 51.22) * mm});
            skSolve(sketch);
        }
        {
            var Q0;
            {var subQ0=sQuery(id+"F18.wireOp",EDGE,"E111.0");var subQ1=sQuery(id+"F18.wireOp",EDGE,"E110.0");var subQ2=makeQuery(id+"F18.imprint","INTERSECT",VERTEX,{"derivedFrom":[subQ1,subQ0]});Q0=makeQuery(id+"F18.imprint","IMPRINT",FACE,{"disambiguationData":[TD([[makeQuery(id+"F18.imprint","IMPRINT",EDGE,{"disambiguationData":[TD([[subQ2,-1.0]])],"derivedFrom":subQ1}),1.0]])]});}
            extrude(context, id + "F19", {"entities" : qUnion([Q0]), "operationType" : NewBodyOperationType.REMOVE, "endBound" : BoundingType.THROUGH_ALL, "oppositeDirection" : true, "depth" : 25.4 * mm, "offsetDistance" : 25.4 * mm});
        }
        {
            var Q0;
            Q0=makeQuery(id+"F3.opExtrude","SWEPT_FACE",FACE,{"disambiguationData":[OSD([sQuery(id+"F2.wireOp",EDGE,"E50")])]});
            var sketch = newSketch(context, id + "F20", { "sketchPlane" : qUnion([Q0])});
            skLineSegment(sketch, "E114", {"start": v(0, 50) * mm, "end": v(0, 0) * mm});
            skSolve(sketch);
        }
        {
            var Q0;
            Q0=sQuery(id+"F20.wireOp",EDGE,"E114");
            var Q1;
            {var subQ0=sQuery(id+"F20.wireOp",EDGE,"E114");Q1=makeQuery(id+"F20.imprint","IMPRINT",FACE,{"disambiguationData":[TD([[makeQuery(id+"F20.imprint","IMPRINT",EDGE,{"derivedFrom":subQ0}),1.0]])]});}
            cPlane(context, id + "F21", {"entities" : qUnion([Q0, Q1]), "cplaneType" : CPlaneType.LINE_ANGLE, "offset" : 25.4 * mm, "angle" : 90 * degree, "width" : 152.4 * mm, "height" : 152.4 * mm});
        }
        {
            var Q0;
            Q0=qCreatedBy(id+"F21.planeOp",FACE);
            var sketch = newSketch(context, id + "F22", { "sketchPlane" : qUnion([Q0])});
            skLineSegment(sketch, "E115.0", {"start": v(-40.68, 36.95) * mm, "end": v(-34.33, 36.95) * mm});
            skLineSegment(sketch, "E116.0", {"start": v(-15.68, 36.95) * mm, "end": v(-9.33, 36.95) * mm});
            skLineSegment(sketch, "E117", {"start": v(-9.33, 36.95) * mm, "end": v(-9.33, 9.96) * mm});
            skLineSegment(sketch, "E118", {"start": v(-15.68, 9.96) * mm, "end": v(-15.68, 36.95) * mm});
            skLineSegment(sketch, "E119", {"start": v(-34.33, 36.95) * mm, "end": v(-34.33, 9.96) * mm});
            skLineSegment(sketch, "E120", {"start": v(-40.68, 9.96) * mm, "end": v(-40.68, 36.95) * mm});
            skLineSegment(sketch, "E121.0.0", {"start": v(0, 9.96) * mm, "end": v(-50, 9.96) * mm});
            skLineSegment(sketch, "E121.0.2", {"start": v(-50, 9.96) * mm, "end": v(0, 9.96) * mm});
            skLineSegment(sketch, "E122", {"start": v(-31.15, 41.57) * mm, "end": v(-31.15, 22.52) * mm});
            skLineSegment(sketch, "E123", {"start": v(-43.85, 22.52) * mm, "end": v(-43.85, 41.57) * mm});
            skLineSegment(sketch, "E124", {"start": v(-6.15, 41.57) * mm, "end": v(-6.15, 22.52) * mm});
            skLineSegment(sketch, "E125", {"start": v(-18.85, 22.52) * mm, "end": v(-18.85, 41.57) * mm});
            skLineSegment(sketch, "E126", {"start": v(-50, 28.87) * mm, "end": v(0, 28.87) * mm});
            skLineSegment(sketch, "E127", {"start": v(-43.85, 41.57) * mm, "end": v(-31.15, 41.57) * mm});
            skLineSegment(sketch, "E128", {"start": v(-18.85, 41.57) * mm, "end": v(-6.15, 41.57) * mm});
            skLineSegment(sketch, "E129.0", {"start": v(-50, 22.52) * mm, "end": v(0, 22.52) * mm});
            skLineSegment(sketch, "E130", {"start": v(-37.5, 41.57) * mm, "end": v(-37.5, 9.96) * mm});
            skLineSegment(sketch, "E131", {"start": v(-12.5, 41.57) * mm, "end": v(-12.5, 9.96) * mm});
            skSolve(sketch);
        }
        {
            var Q0;
            {var subQ3=sQuery(id+"F22.wireOp",EDGE,"E120");var subQ8=sQuery(id+"F22.wireOp",EDGE,"E115.0");var subQ11=makeQuery(id+"F22.imprint","INTERSECT",VERTEX,{"derivedFrom":[subQ8,subQ3]});Q0=makeQuery(id+"F22.imprint","IMPRINT",FACE,{"disambiguationData":[TD([[makeQuery(id+"F22.imprint","IMPRINT",EDGE,{"disambiguationData":[TD([[subQ11,-1.0]])],"derivedFrom":subQ8}),1.0]])]});}
            var Q1;
            {var subQ0=sQuery(id+"F22.wireOp",EDGE,"E120");var subQ1=sQuery(id+"F22.wireOp",EDGE,"E115.0");var subQ2=makeQuery(id+"F22.imprint","INTERSECT",VERTEX,{"derivedFrom":[subQ1,subQ0]});Q1=makeQuery(id+"F22.imprint","IMPRINT",FACE,{"disambiguationData":[TD([[makeQuery(id+"F22.imprint","IMPRINT",EDGE,{"disambiguationData":[TD([[subQ2,-1.0]])],"derivedFrom":subQ1}),-1.0]])]});}
            var Q2;
            {var subQ0=sQuery(id+"F22.wireOp",EDGE,"E121.0.2");var subQ1=sQuery(id+"F22.wireOp",EDGE,"E120");var subQ2=makeQuery(id+"F22.imprint","INTERSECT",VERTEX,{"derivedFrom":[subQ1,subQ0]});Q2=makeQuery(id+"F22.imprint","IMPRINT",FACE,{"disambiguationData":[TD([[makeQuery(id+"F22.imprint","IMPRINT",EDGE,{"disambiguationData":[TD([[subQ2,-1.0]])],"derivedFrom":subQ1}),-1.0]])]});}
            var Q3;
            {var subQ0=sQuery(id+"F22.wireOp",EDGE,"E129.0");var subQ1=sQuery(id+"F22.wireOp",EDGE,"E120");var subQ2=makeQuery(id+"F22.imprint","INTERSECT",VERTEX,{"derivedFrom":[subQ1,subQ0]});Q3=makeQuery(id+"F22.imprint","IMPRINT",FACE,{"disambiguationData":[TD([[makeQuery(id+"F22.imprint","IMPRINT",EDGE,{"disambiguationData":[TD([[subQ2,-1.0]])],"derivedFrom":subQ1}),-1.0]])]});}
            var Q4;
            {var subQ0=sQuery(id+"F22.wireOp",EDGE,"E129.0");var subQ1=sQuery(id+"F22.wireOp",EDGE,"E120");var subQ2=makeQuery(id+"F22.imprint","INTERSECT",VERTEX,{"derivedFrom":[subQ1,subQ0]});Q4=makeQuery(id+"F22.imprint","IMPRINT",FACE,{"disambiguationData":[TD([[makeQuery(id+"F22.imprint","IMPRINT",EDGE,{"disambiguationData":[TD([[subQ2,-1.0]])],"derivedFrom":subQ1}),1.0]])]});}
            var Q5;
            Q5=sQuery(id+"F22.wireOp",EDGE,"E130");
            revolve(context, id + "F23", {"operationType" : NewBodyOperationType.REMOVE, "entities" : qUnion([Q0, Q1, Q2, Q3, Q4]), "axis" : qUnion([Q5]), "revolveType" : RevolveType.FULL, "oppositeDirection" : true});
        }
        {
            var Q0;
            {var subQ0=sQuery(id+"F22.wireOp",EDGE,"E129.0");var subQ1=sQuery(id+"F22.wireOp",EDGE,"E118");var subQ2=makeQuery(id+"F22.imprint","INTERSECT",VERTEX,{"derivedFrom":[subQ1,subQ0]});Q0=makeQuery(id+"F22.imprint","IMPRINT",FACE,{"disambiguationData":[TD([[makeQuery(id+"F22.imprint","IMPRINT",EDGE,{"disambiguationData":[TD([[subQ2,-1.0]])],"derivedFrom":subQ1}),1.0]])]});}
            var Q1;
            {var subQ0=sQuery(id+"F22.wireOp",EDGE,"E129.0");var subQ1=sQuery(id+"F22.wireOp",EDGE,"E118");var subQ2=makeQuery(id+"F22.imprint","INTERSECT",VERTEX,{"derivedFrom":[subQ1,subQ0]});Q1=makeQuery(id+"F22.imprint","IMPRINT",FACE,{"disambiguationData":[TD([[makeQuery(id+"F22.imprint","IMPRINT",EDGE,{"disambiguationData":[TD([[subQ2,-1.0]])],"derivedFrom":subQ1}),-1.0]])]});}
            var Q2;
            {var subQ0=sQuery(id+"F22.wireOp",EDGE,"E121.0.2");var subQ1=sQuery(id+"F22.wireOp",EDGE,"E118");var subQ2=makeQuery(id+"F22.imprint","INTERSECT",VERTEX,{"derivedFrom":[subQ1,subQ0]});Q2=makeQuery(id+"F22.imprint","IMPRINT",FACE,{"disambiguationData":[TD([[makeQuery(id+"F22.imprint","IMPRINT",EDGE,{"disambiguationData":[TD([[subQ2,-1.0]])],"derivedFrom":subQ1}),-1.0]])]});}
            var Q3;
            {var subQ5=sQuery(id+"F22.wireOp",EDGE,"E118");var subQ7=sQuery(id+"F22.wireOp",EDGE,"E116.0");var subQ8=makeQuery(id+"F22.imprint","INTERSECT",VERTEX,{"derivedFrom":[subQ7,subQ5]});Q3=makeQuery(id+"F22.imprint","IMPRINT",FACE,{"disambiguationData":[TD([[makeQuery(id+"F22.imprint","IMPRINT",EDGE,{"disambiguationData":[TD([[subQ8,-1.0]])],"derivedFrom":subQ7}),1.0]])]});}
            var Q4;
            {var subQ0=sQuery(id+"F22.wireOp",EDGE,"E118");var subQ1=sQuery(id+"F22.wireOp",EDGE,"E116.0");var subQ2=makeQuery(id+"F22.imprint","INTERSECT",VERTEX,{"derivedFrom":[subQ1,subQ0]});Q4=makeQuery(id+"F22.imprint","IMPRINT",FACE,{"disambiguationData":[TD([[makeQuery(id+"F22.imprint","IMPRINT",EDGE,{"disambiguationData":[TD([[subQ2,-1.0]])],"derivedFrom":subQ1}),-1.0]])]});}
            var Q5;
            Q5=sQuery(id+"F22.wireOp",EDGE,"E131");
            revolve(context, id + "F24", {"operationType" : NewBodyOperationType.REMOVE, "entities" : qUnion([Q0, Q1, Q2, Q3, Q4]), "axis" : qUnion([Q5]), "revolveType" : RevolveType.FULL, "oppositeDirection" : true});
        }
        {
            var Q0;
            Q0=makeQuery(id+"F1.opExtrude","SWEPT_BODY",BODY,{"disambiguationData":[OSD([sQuery(id+"F0.wireOp",EDGE,"E8"),sQuery(id+"F0.wireOp",EDGE,"E9"),sQuery(id+"F0.wireOp",EDGE,"E14"),sQuery(id+"F0.wireOp",EDGE,"E15"),sQuery(id+"F0.wireOp",EDGE,"E16"),sQuery(id+"F0.wireOp",EDGE,"E17"),sQuery(id+"F0.wireOp",EDGE,"E20"),sQuery(id+"F0.wireOp",EDGE,"E21"),sQuery(id+"F0.wireOp",EDGE,"E23"),sQuery(id+"F0.wireOp",EDGE,"E24"),sQuery(id+"F0.wireOp",EDGE,"E28"),sQuery(id+"F0.wireOp",EDGE,"E29"),sQuery(id+"F0.wireOp",EDGE,"E30"),sQuery(id+"F0.wireOp",EDGE,"E31")])]});
            var Q1;
            {var subQ0=sQuery(id+"F2.wireOp",EDGE,"E36.0");var subQ1=makeQuery(id+"F3.opExtrude","CAP_FACE",FACE,{"disambiguationData":[OSD([subQ0,sQuery(id+"F2.wireOp",EDGE,"E39"),sQuery(id+"F2.wireOp",EDGE,"E40"),sQuery(id+"F2.wireOp",EDGE,"E41")])],"isStart":false});var subQ5=sQuery(id+"F0.wireOp",EDGE,"E20");var subQ7=sQuery(id+"F0.wireOp",EDGE,"E28");var subQ11=sQuery(id+"F2.wireOp",EDGE,"E43");Q1=makeQuery(id+"F10.boolean.opBoolean","SPLIT",FACE,{"disambiguationData":[TD([subQ1])],"derivedFrom":makeQuery(id+"F9.boolean.opBoolean","SPLIT",FACE,{"disambiguationData":[TD([subQ1])],"derivedFrom":makeQuery(id+"F3.boolean.opBoolean","MERGE",FACE,{"derivedFrom":[makeQuery(id+"F1.opExtrude","SWEPT_FACE",FACE,{"disambiguationData":[OSD([subQ7]),TDD([makeQuery(id+"F0.imprint","IMPRINT",EDGE,{"disambiguationData":[TD([[makeQuery(id+"F0.imprint","INTERSECT",VERTEX,{"derivedFrom":[subQ5,subQ7]}),1.0]])],"derivedFrom":subQ7})])]}),makeQuery(id+"F3.opExtrude","SWEPT_FACE",FACE,{"disambiguationData":[OSD([subQ11])]})]})})});}
            mirror(context, id + "F25", {"operationType" : NewBodyOperationType.ADD, "entities" : qUnion([Q0]), "mirrorPlane" : qUnion([Q1])});
        }
    });
